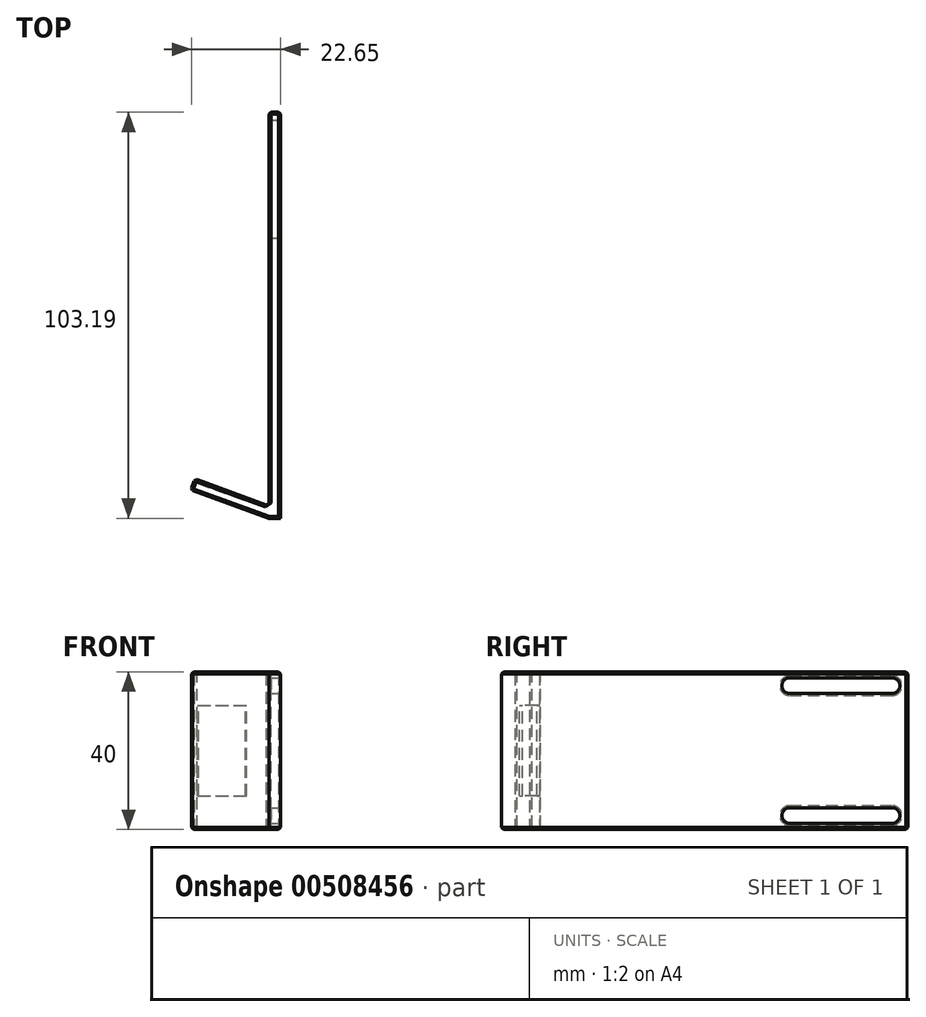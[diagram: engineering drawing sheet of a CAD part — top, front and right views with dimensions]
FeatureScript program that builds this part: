
annotation { "Feature Type Name" : "Feature", "Feature Type Description" : "" }
export const myFeature = defineFeature(function(context is Context, id is Id, definition is map)
    precondition{}
    {
        {
            var Q0;
            Q0=qCreatedBy(makeId("Top.planeOp"),FACE);
            var sketch = newSketch(context, id + "F0", { "sketchPlane" : qUnion([Q0])});
            skLineSegment(sketch, "E0.bottom", {"start": v(0, 50) * mm, "end": v(3, 50) * mm});
            skLineSegment(sketch, "E0.top", {"start": v(0, -50) * mm, "end": v(3, -50) * mm});
            skLineSegment(sketch, "E0.left", {"start": v(0, 50) * mm, "end": v(0, -50) * mm});
            skLineSegment(sketch, "E0.right", {"start": v(3, 50) * mm, "end": v(3, -50) * mm});
            skLineSegment(sketch, "E1", {"start": v(0, -50) * mm, "end": v(-18.8, -43.16) * mm});
            skLineSegment(sketch, "E2", {"start": v(-18.8, -43.16) * mm, "end": v(-19.82, -45.98) * mm});
            skLineSegment(sketch, "E3", {"start": v(-19.82, -45.98) * mm, "end": v(0, -53.2) * mm});
            skLineSegment(sketch, "E4", {"start": v(0, -53.2) * mm, "end": v(3, -53.2) * mm});
            skLineSegment(sketch, "E5", {"start": v(3, -53.2) * mm, "end": v(3, -50) * mm});
            skSolve(sketch);
        }
        {
            var Q0;
            Q0=qSketchRegion(id+"F0",true);
            extrude(context, id + "F1", {"entities" : qUnion([Q0]), "depth" : 40 * mm, "offsetDistance" : 25 * mm});
        }
        {
            var Q0;
            Q0=makeQuery(id+"F1.opExtrude","SWEPT_FACE",FACE,{"disambiguationData":[OSD([sQuery(id+"F0.wireOp",EDGE,"E0.right"),sQuery(id+"F0.wireOp",EDGE,"E5")])]});
            var sketch = newSketch(context, id + "F2", { "sketchPlane" : qUnion([Q0])});
            skLineSegment(sketch, "E6.bottom", {"start": v(46, 38.5) * mm, "end": v(20, 38.5) * mm});
            skLineSegment(sketch, "E6.top", {"start": v(46, 34.5) * mm, "end": v(20, 34.5) * mm});
            skLineSegment(sketch, "E6.left", {"start": v(46, 38.5) * mm, "end": v(46, 34.5) * mm});
            skLineSegment(sketch, "E6.right", {"start": v(20, 38.5) * mm, "end": v(20, 34.5) * mm});
            skCircle(sketch, "E7", {"center": v(46, 36.5) * mm, "radius": 2 * mm});
            skCircle(sketch, "E8", {"center": v(20, 36.5) * mm, "radius": 2 * mm});
            skLineSegment(sketch, "E9.bottom", {"start": v(20, 5.5) * mm, "end": v(46, 5.5) * mm});
            skLineSegment(sketch, "E9.top", {"start": v(20, 1.5) * mm, "end": v(46, 1.5) * mm});
            skLineSegment(sketch, "E9.left", {"start": v(20, 5.5) * mm, "end": v(20, 1.5) * mm});
            skLineSegment(sketch, "E9.right", {"start": v(46, 5.5) * mm, "end": v(46, 1.5) * mm});
            skCircle(sketch, "E10", {"center": v(20, 3.5) * mm, "radius": 2 * mm});
            skCircle(sketch, "E11", {"center": v(46, 3.5) * mm, "radius": 2 * mm});
            skSolve(sketch);
        }
        {
            var Q0;
            {var subQ0=sQuery(id+"F2.wireOp",EDGE,"E6.bottom");Q0=makeQuery(id+"F2.imprint","IMPRINT",FACE,{"disambiguationData":[TD([[makeQuery(id+"F2.imprint","IMPRINT",EDGE,{"derivedFrom":subQ0}),1.0]])]});}
            var Q1;
            {var subQ0=sQuery(id+"F2.wireOp",EDGE,"E6.left");Q1=makeQuery(id+"F2.imprint","IMPRINT",FACE,{"disambiguationData":[TD([[makeQuery(id+"F2.imprint","IMPRINT",EDGE,{"derivedFrom":subQ0}),-1.0]])]});}
            var Q2;
            {var subQ0=sQuery(id+"F2.wireOp",EDGE,"E6.left");Q2=makeQuery(id+"F2.imprint","IMPRINT",FACE,{"disambiguationData":[TD([[makeQuery(id+"F2.imprint","IMPRINT",EDGE,{"derivedFrom":subQ0}),1.0]])]});}
            var Q3;
            {var subQ0=sQuery(id+"F2.wireOp",EDGE,"E6.right");Q3=makeQuery(id+"F2.imprint","IMPRINT",FACE,{"disambiguationData":[TD([[makeQuery(id+"F2.imprint","IMPRINT",EDGE,{"derivedFrom":subQ0}),1.0]])]});}
            var Q4;
            {var subQ0=sQuery(id+"F2.wireOp",EDGE,"E6.right");Q4=makeQuery(id+"F2.imprint","IMPRINT",FACE,{"disambiguationData":[TD([[makeQuery(id+"F2.imprint","IMPRINT",EDGE,{"derivedFrom":subQ0}),-1.0]])]});}
            var Q5;
            {var subQ0=sQuery(id+"F2.wireOp",EDGE,"E9.bottom");Q5=makeQuery(id+"F2.imprint","IMPRINT",FACE,{"disambiguationData":[TD([[makeQuery(id+"F2.imprint","IMPRINT",EDGE,{"derivedFrom":subQ0}),-1.0]])]});}
            var Q6;
            {var subQ0=sQuery(id+"F2.wireOp",EDGE,"E9.left");Q6=makeQuery(id+"F2.imprint","IMPRINT",FACE,{"disambiguationData":[TD([[makeQuery(id+"F2.imprint","IMPRINT",EDGE,{"derivedFrom":subQ0}),1.0]])]});}
            var Q7;
            {var subQ0=sQuery(id+"F2.wireOp",EDGE,"E9.left");Q7=makeQuery(id+"F2.imprint","IMPRINT",FACE,{"disambiguationData":[TD([[makeQuery(id+"F2.imprint","IMPRINT",EDGE,{"derivedFrom":subQ0}),-1.0]])]});}
            var Q8;
            {var subQ0=sQuery(id+"F2.wireOp",EDGE,"E9.right");Q8=makeQuery(id+"F2.imprint","IMPRINT",FACE,{"disambiguationData":[TD([[makeQuery(id+"F2.imprint","IMPRINT",EDGE,{"derivedFrom":subQ0}),-1.0]])]});}
            var Q9;
            {var subQ0=sQuery(id+"F2.wireOp",EDGE,"E9.right");Q9=makeQuery(id+"F2.imprint","IMPRINT",FACE,{"disambiguationData":[TD([[makeQuery(id+"F2.imprint","IMPRINT",EDGE,{"derivedFrom":subQ0}),1.0]])]});}
            extrude(context, id + "F3", {"entities" : qUnion([Q0, Q1, Q2, Q3, Q4, Q5, Q6, Q7, Q8, Q9]), "operationType" : NewBodyOperationType.REMOVE, "oppositeDirection" : true, "depth" : 25 * mm, "offsetDistance" : 25 * mm});
        }
        {
            var Q0;
            Q0=makeQuery(id+"F1.opExtrude","SWEPT_FACE",FACE,{"disambiguationData":[OSD([sQuery(id+"F0.wireOp",EDGE,"E1")])]});
            var sketch = newSketch(context, id + "F4", { "sketchPlane" : qUnion([Q0])});
            skLineSegment(sketch, "E12.bottom", {"start": v(1.9, 8.5) * mm, "end": v(-11.1, 8.5) * mm});
            skLineSegment(sketch, "E12.top", {"start": v(1.9, 31.5) * mm, "end": v(-11.1, 31.5) * mm});
            skLineSegment(sketch, "E12.left", {"start": v(1.9, 8.5) * mm, "end": v(1.9, 31.5) * mm});
            skLineSegment(sketch, "E12.right", {"start": v(-11.1, 8.5) * mm, "end": v(-11.1, 31.5) * mm});
            skSolve(sketch);
        }
        {
            var Q0;
            Q0=makeQuery(id+"F4.imprint","IMPRINT",FACE,{"disambiguationData":[TD([[makeQuery(id+"F4.imprint","IMPRINT",EDGE,{"derivedFrom":sQuery(id+"F4.wireOp",EDGE,"E12.bottom")}),-1.0]])]});
            extrude(context, id + "F5", {"entities" : qUnion([Q0]), "operationType" : NewBodyOperationType.REMOVE, "oppositeDirection" : true, "depth" : .8 * mm, "offsetDistance" : 25 * mm});
        }
        {
            var Q0;
            Q0=makeQuery(id+"F1.opExtrude","CAP_FACE",FACE,{"disambiguationData":[OSD([sQuery(id+"F0.wireOp",EDGE,"E0.bottom"),sQuery(id+"F0.wireOp",EDGE,"E0.left"),sQuery(id+"F0.wireOp",EDGE,"E0.right"),sQuery(id+"F0.wireOp",EDGE,"E1"),sQuery(id+"F0.wireOp",EDGE,"E2"),sQuery(id+"F0.wireOp",EDGE,"E3"),sQuery(id+"F0.wireOp",EDGE,"E4"),sQuery(id+"F0.wireOp",EDGE,"E5")])],"isStart":false});
            var Q1;
            Q1=makeQuery(id+"F1.opExtrude","SWEPT_FACE",FACE,{"disambiguationData":[OSD([sQuery(id+"F0.wireOp",EDGE,"E0.bottom")])]});
            var Q2;
            Q2=makeQuery(id+"F1.opExtrude","CAP_FACE",FACE,{"disambiguationData":[OSD([sQuery(id+"F0.wireOp",EDGE,"E0.bottom"),sQuery(id+"F0.wireOp",EDGE,"E0.left"),sQuery(id+"F0.wireOp",EDGE,"E0.right"),sQuery(id+"F0.wireOp",EDGE,"E1"),sQuery(id+"F0.wireOp",EDGE,"E2"),sQuery(id+"F0.wireOp",EDGE,"E3"),sQuery(id+"F0.wireOp",EDGE,"E4"),sQuery(id+"F0.wireOp",EDGE,"E5")])],"isStart":true});
            var Q3;
            Q3=makeQuery(id+"F1.opExtrude","SWEPT_FACE",FACE,{"disambiguationData":[OSD([sQuery(id+"F0.wireOp",EDGE,"E2")])]});
            var Q4;
            Q4=makeQuery(id+"F3.boolean.opBoolean","INTERSECT",EDGE,{"derivedFrom":[makeQuery(id+"F1.opExtrude","SWEPT_FACE",FACE,{"disambiguationData":[OSD([sQuery(id+"F0.wireOp",EDGE,"E0.left")])]}),makeQuery(id+"F3.opExtrude","SWEPT_FACE",FACE,{"disambiguationData":[OSD([sQuery(id+"F2.wireOp",EDGE,"E8")])]})]});
            var Q5;
            Q5=makeQuery(id+"F1.opExtrude","SWEPT_FACE",FACE,{"disambiguationData":[OSD([sQuery(id+"F0.wireOp",EDGE,"E0.left")])]});
            var Q6;
            Q6=makeQuery(id+"F3.boolean.opBoolean","COPY",EDGE,{"derivedFrom":makeQuery(id+"F3.opExtrude","CAP_EDGE",EDGE,{"disambiguationData":[OSD([sQuery(id+"F2.wireOp",EDGE,"E9.bottom")])],"isStart":true})});
            var Q7;
            Q7=makeQuery(id+"F3.boolean.opBoolean","COPY",EDGE,{"derivedFrom":makeQuery(id+"F3.opExtrude","CAP_EDGE",EDGE,{"disambiguationData":[OSD([sQuery(id+"F2.wireOp",EDGE,"E6.top")])],"isStart":true})});
            chamfer(context, id + "F6", {"entities" : qUnion([Q0, Q1, Q2, Q3, Q4, Q5, Q6, Q7]), "width" : .5 * mm, "tangentPropagation" : true});
        }
    });
